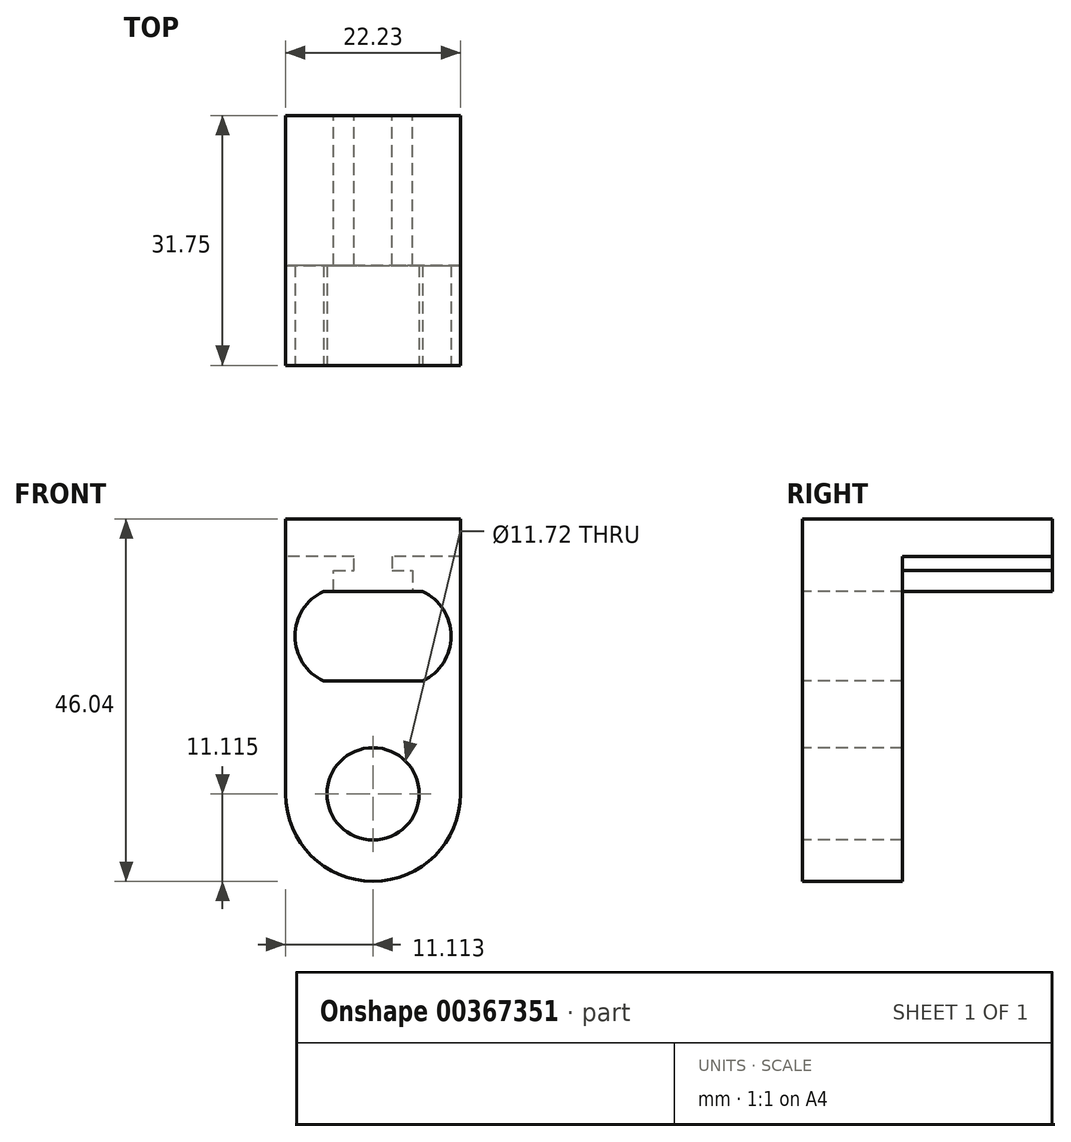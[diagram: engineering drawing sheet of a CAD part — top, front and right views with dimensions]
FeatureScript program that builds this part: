
annotation { "Feature Type Name" : "Feature", "Feature Type Description" : "" }
export const myFeature = defineFeature(function(context is Context, id is Id, definition is map)
    precondition{}
    {
        {
            var Q0;
            Q0=qCreatedBy(makeId("Front.planeOp"),FACE);
            var sketch = newSketch(context, id + "F0", { "sketchPlane" : qUnion([Q0])});
            skLineSegment(sketch, "E0", {"start": v(0, 0) * mm, "end": v(22.22, 0) * mm});
            skLineSegment(sketch, "E1", {"start": v(22.23, 0) * mm, "end": v(22.23, -4.76) * mm});
            skLineSegment(sketch, "E2", {"start": v(22.22, -4.76) * mm, "end": v(13.53, -4.76) * mm});
            skLineSegment(sketch, "E3", {"start": v(13.53, -4.76) * mm, "end": v(13.53, -6.54) * mm});
            skLineSegment(sketch, "E4", {"start": v(13.53, -6.54) * mm, "end": v(16.13, -6.54) * mm});
            skLineSegment(sketch, "E5", {"start": v(16.13, -6.54) * mm, "end": v(16.13, -9.2) * mm});
            skLineSegment(sketch, "E6", {"start": v(16.13, -9.2) * mm, "end": v(6.1, -9.2) * mm});
            skLineSegment(sketch, "E7", {"start": v(6.1, -9.2) * mm, "end": v(6.1, -6.54) * mm});
            skLineSegment(sketch, "E8", {"start": v(6.1, -6.54) * mm, "end": v(8.7, -6.54) * mm});
            skLineSegment(sketch, "E9", {"start": v(8.7, -6.54) * mm, "end": v(8.7, -4.76) * mm});
            skLineSegment(sketch, "E10", {"start": v(8.7, -4.76) * mm, "end": v(0, -4.76) * mm});
            skLineSegment(sketch, "E11", {"start": v(0, -4.76) * mm, "end": v(0, 0) * mm});
            skSolve(sketch);
        }
        {
            var Q0;
            Q0=makeQuery(id+"F0.imprint","IMPRINT",FACE,{"disambiguationData":[TD([[makeQuery(id+"F0.imprint","IMPRINT",EDGE,{"derivedFrom":sQuery(id+"F0.wireOp",EDGE,"E0")}),-1.0]])]});
            extrude(context, id + "F1", {"entities" : qUnion([Q0]), "depth" : 19.05 * mm});
        }
        {
            var Q0;
            Q0=makeQuery(id+"F1.opExtrude","CAP_FACE",FACE,{"disambiguationData":[OSD([sQuery(id+"F0.wireOp",EDGE,"E0"),sQuery(id+"F0.wireOp",EDGE,"E1"),sQuery(id+"F0.wireOp",EDGE,"E2"),sQuery(id+"F0.wireOp",EDGE,"E3"),sQuery(id+"F0.wireOp",EDGE,"E4"),sQuery(id+"F0.wireOp",EDGE,"E5"),sQuery(id+"F0.wireOp",EDGE,"E6"),sQuery(id+"F0.wireOp",EDGE,"E7"),sQuery(id+"F0.wireOp",EDGE,"E8"),sQuery(id+"F0.wireOp",EDGE,"E9"),sQuery(id+"F0.wireOp",EDGE,"E10"),sQuery(id+"F0.wireOp",EDGE,"E11")])],"isStart":false});
            var sketch = newSketch(context, id + "F2", { "sketchPlane" : qUnion([Q0])});
            skLineSegment(sketch, "E12", {"start": v(0, 0) * mm, "end": v(0, -34.93) * mm});
            skLineSegment(sketch, "E13", {"start": v(22.23, 0) * mm, "end": v(22.23, -34.93) * mm});
            skPoint(sketch, "E13.endSnap0", {"position": v(22.23, -2.38) * mm});
            skArc(sketch, "E14", {"start": v(0, -34.93) * mm, "mid": v(11.11, -46.04) * mm, "end": v(22.23, -34.93) * mm});
            skSolve(sketch);
        }
        {
            var Q0;
            {var subQ2=sQuery(id+"F2.wireOp",EDGE,"E14");Q0=makeQuery(id+"F2.imprint","IMPRINT",FACE,{"disambiguationData":[TD([[makeQuery(id+"F2.imprint","IMPRINT",EDGE,{"derivedFrom":subQ2}),1.0]])]});}
            var Q1;
            {var subQ1=makeQuery(id+"F1.opExtrude","CAP_EDGE",EDGE,{"disambiguationData":[OSD([sQuery(id+"F0.wireOp",EDGE,"E0")])],"isStart":false});Q1=makeQuery(id+"F2.imprint","IMPRINT",FACE,{"disambiguationData":[TD([[makeQuery(id+"F2.imprint","IMPRINT",EDGE,{"derivedFrom":subQ1}),-1.0]])]});}
            extrude(context, id + "F3", {"entities" : qUnion([Q0, Q1]), "operationType" : NewBodyOperationType.ADD, "depth" : 12.7 * mm});
        }
        {
            var Q0;
            Q0=makeQuery(id+"F3.opExtrude","CAP_FACE",FACE,{"disambiguationData":[OSD([sQuery(id+"F0.wireOp",EDGE,"E0"),sQuery(id+"F2.wireOp",EDGE,"E12"),sQuery(id+"F2.wireOp",EDGE,"E13"),sQuery(id+"F2.wireOp",EDGE,"E14")])],"isStart":false});
            var sketch = newSketch(context, id + "F4", { "sketchPlane" : qUnion([Q0])});
            skCircle(sketch, "E15", {"center": v(11.11, -34.93) * mm, "radius": 5.86 * mm});
            skCircle(sketch, "E16", {"center": v(11.11, -34.93) * mm, "radius": 5.56 * mm, "construction": true});
            skSolve(sketch);
        }
        {
            var Q0;
            Q0=makeQuery(id+"F4.imprint","IMPRINT",FACE,{"disambiguationData":[TD([[makeQuery(id+"F4.imprint","IMPRINT",EDGE,{"derivedFrom":sQuery(id+"F4.wireOp",EDGE,"E15")}),1.0]])]});
            var Q1;
            Q1=sQuery(id+"F4.wireOp",EDGE,"E15");
            extrude(context, id + "F5", {"entities" : qUnion([Q0]), "operationType" : NewBodyOperationType.REMOVE, "surfaceEntities" : qUnion([Q1]), "oppositeDirection" : true, "depth" : 25.4 * mm});
        }
        {
            var Q0;
            Q0=makeQuery(id+"F3.opExtrude","CAP_FACE",FACE,{"disambiguationData":[OSD([sQuery(id+"F0.wireOp",EDGE,"E0"),sQuery(id+"F2.wireOp",EDGE,"E12"),sQuery(id+"F2.wireOp",EDGE,"E13"),sQuery(id+"F2.wireOp",EDGE,"E14")])],"isStart":false});
            var sketch = newSketch(context, id + "F6", { "sketchPlane" : qUnion([Q0])});
            skLineSegment(sketch, "E17", {"start": v(4.83, -9.2) * mm, "end": v(17.4, -9.2) * mm});
            skLineSegment(sketch, "E18", {"start": v(4.83, -20.58) * mm, "end": v(17.4, -20.58) * mm});
            skArc(sketch, "E19", {"start": v(4.83, -9.2) * mm, "mid": v(1.2, -14.9) * mm, "end": v(4.83, -20.58) * mm});
            skArc(sketch, "E20", {"start": v(17.4, -20.58) * mm, "mid": v(21.03, -14.9) * mm, "end": v(17.4, -9.2) * mm});
            skSolve(sketch);
        }
        {
            var Q0;
            Q0=makeQuery(id+"F6.imprint","IMPRINT",FACE,{"disambiguationData":[TD([[makeQuery(id+"F6.imprint","IMPRINT",EDGE,{"derivedFrom":sQuery(id+"F6.wireOp",EDGE,"E17")}),-1.0]])]});
            extrude(context, id + "F7", {"entities" : qUnion([Q0]), "operationType" : NewBodyOperationType.REMOVE, "oppositeDirection" : true, "depth" : 25.4 * mm});
        }
    });
